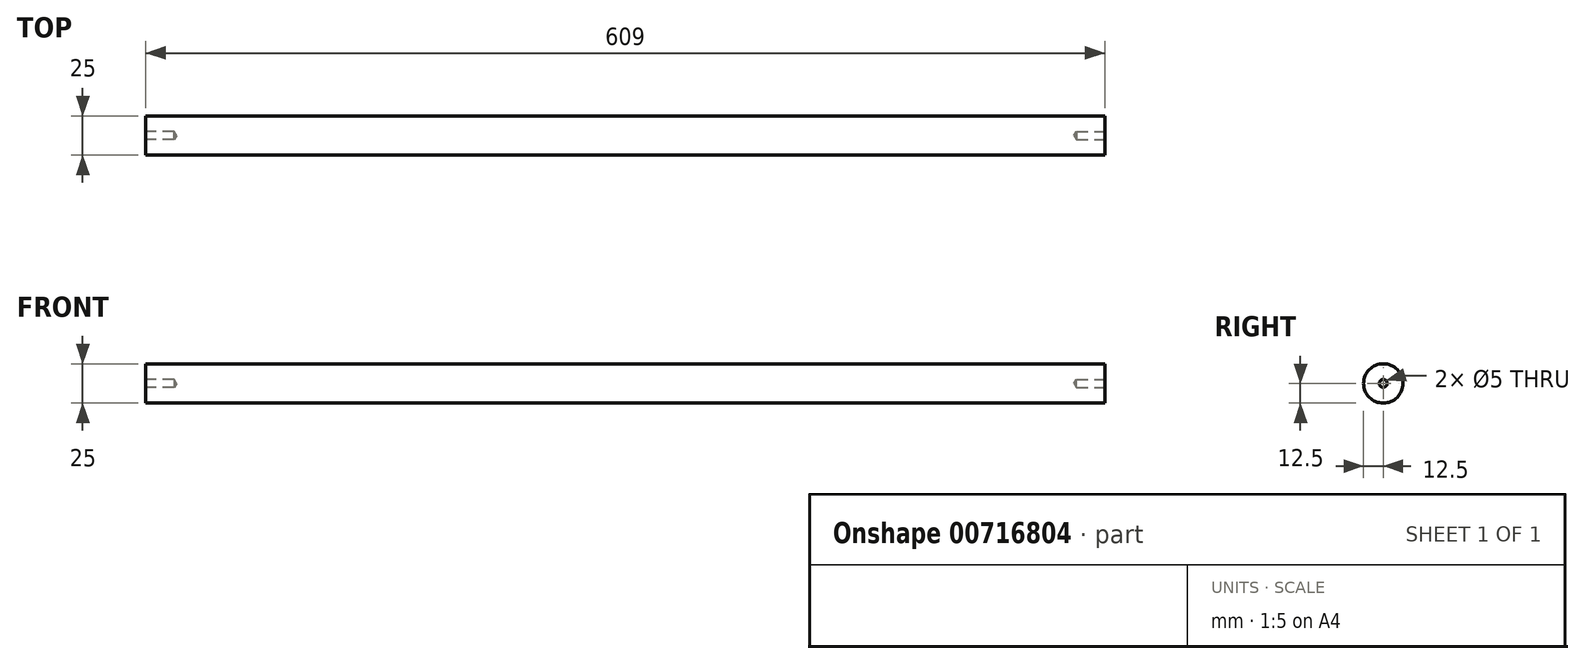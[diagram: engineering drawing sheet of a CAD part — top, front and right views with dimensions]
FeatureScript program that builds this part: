
annotation { "Feature Type Name" : "Feature", "Feature Type Description" : "" }
export const myFeature = defineFeature(function(context is Context, id is Id, definition is map)
    precondition{}
    {
        {
            var Q0;
            Q0=qCreatedBy(makeId("Right.planeOp"),FACE);
            var sketch = newSketch(context, id + "F0", { "sketchPlane" : qUnion([Q0])});
            skCircle(sketch, "E0", {"center": v(0, 0) * mm, "radius": 12.5 * mm});
            skSolve(sketch);
        }
        {
            var Q0;
            Q0 = qSketchRegion(id + "F0", true);
            extrude(context, id + "F1", {"entities" : qUnion([Q0]), "endBound" : BoundingType.SYMMETRIC, "depth" : 609 * mm, "offsetDistance" : 25 * mm});
        }
        {
            var Q0;
            Q0=makeQuery(id+"F1.opExtrude","CAP_FACE",FACE,{"disambiguationData":[OSD([sQuery(id+"F0.wireOp",EDGE,"E0")])],"isStart":false});
            var sketch = newSketch(context, id + "F2", { "sketchPlane" : qUnion([Q0])});
            skPoint(sketch, "E1", {"position": v(0, 0) * mm});
            skSolve(sketch);
        }
        {
            var Q0;
            Q0=makeQuery(id+"F1.opExtrude","CAP_FACE",FACE,{"disambiguationData":[OSD([sQuery(id+"F0.wireOp",EDGE,"E0")])],"isStart":true});
            var sketch = newSketch(context, id + "F3", { "sketchPlane" : qUnion([Q0])});
            skPoint(sketch, "E2", {"position": v(0, 0) * mm});
            skSolve(sketch);
        }
        {
            var Q0;
            Q0=sQuery(id+"F3.wireOp",VERTEX,"E2");
            var Q1;
            Q1=sQuery(id+"F2.wireOp",VERTEX,"E1");
            var Q2;
            Q2=makeQuery(id+"F1.opExtrude","SWEPT_BODY",BODY,{"disambiguationData":[OSD([sQuery(id+"F0.wireOp",EDGE,"E0")])]});
            hole(context, id + "F4", {"style" : HoleStyle.SIMPLE, "endStyle" : HoleEndStyle.BLIND, "standardTappedOrClearance" : lookupTablePath({ "standard" : "ISO", "engagement" : "75%", "pitch" : "1 mm", "size" : "M6", "type" : "Tapped" }), "standardBlindInLast" : lookupTablePath({ "standard" : "ISO", "engagement" : "75%", "pitch" : "1 mm", "size" : "M6", "type" : "Tapped" }), "holeDiameter" : 5 * mm, "majorDiameter" : 6 * mm, "showTappedDepth" : true, "holeDepth" : 18 * mm, "isTappedThrough" : true, "tappedDepth" : 15 * mm, "tapClearance" : 3, "startFromSketch" : true, "locations" : qUnion([Q0, Q1]), "scope" : qUnion([Q2])});
        }
    });
